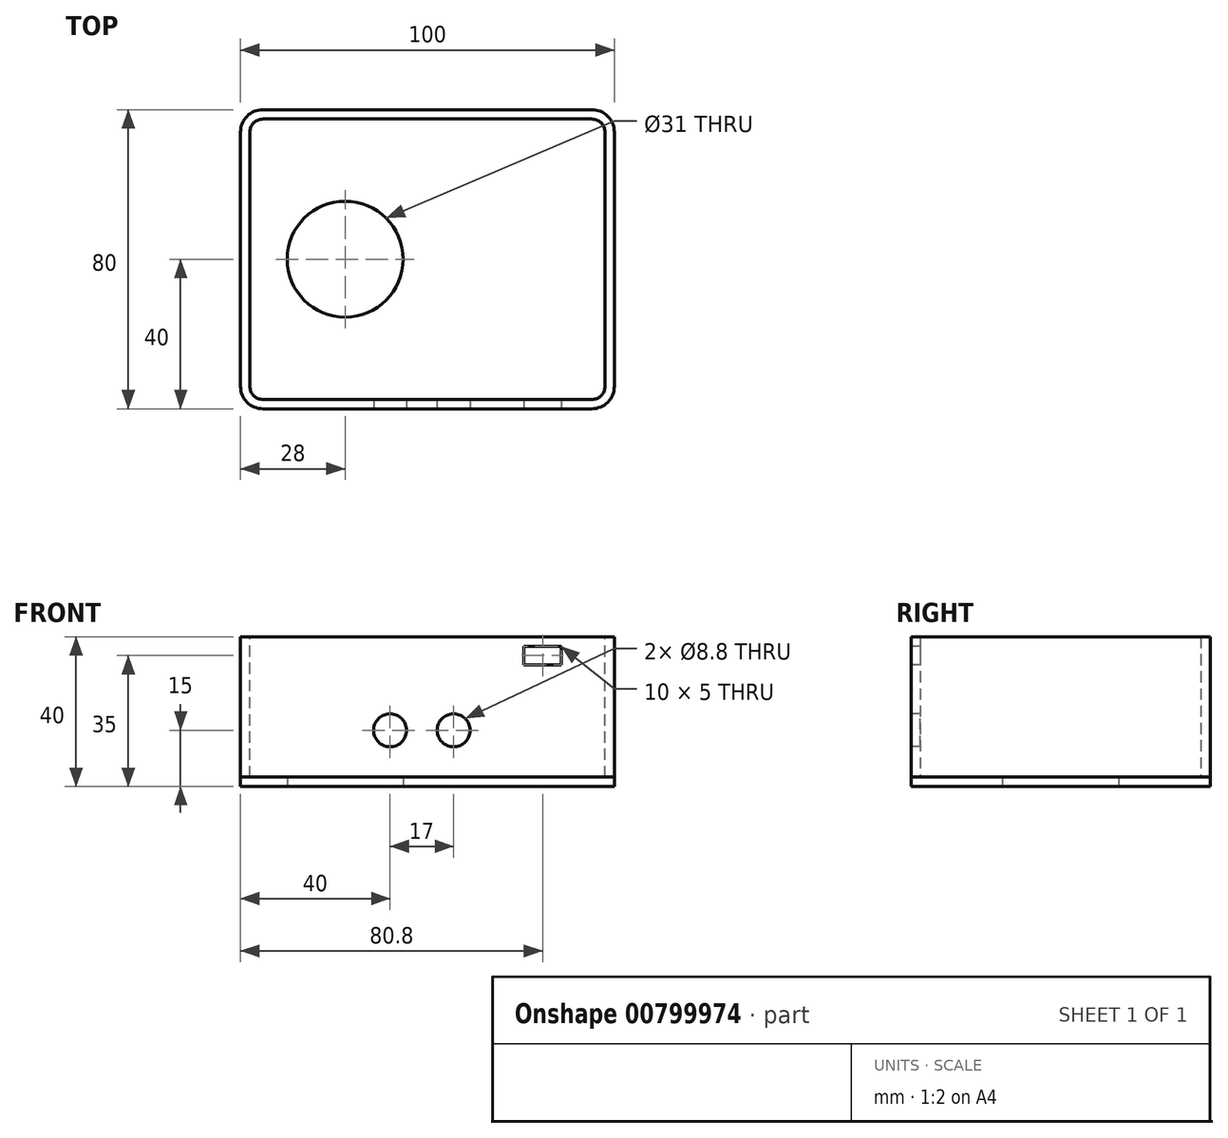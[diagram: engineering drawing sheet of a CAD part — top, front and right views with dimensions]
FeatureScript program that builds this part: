
annotation { "Feature Type Name" : "Feature", "Feature Type Description" : "" }
export const myFeature = defineFeature(function(context is Context, id is Id, definition is map)
    precondition{}
    {
        {
            var Q0;
            Q0=qCreatedBy(makeId("Top.planeOp"),FACE);
            var sketch = newSketch(context, id + "F0", { "sketchPlane" : qUnion([Q0])});
            skLineSegment(sketch, "E0.bottom", {"start": v(50, -40) * mm, "end": v(-50, -40) * mm});
            skLineSegment(sketch, "E0.top", {"start": v(50, 40) * mm, "end": v(-50, 40) * mm});
            skLineSegment(sketch, "E0.left", {"start": v(50, -40) * mm, "end": v(50, 40) * mm});
            skLineSegment(sketch, "E0.right", {"start": v(-50, -40) * mm, "end": v(-50, 40) * mm});
            skPoint(sketch, "E0.middle", {"position": v(0, 0) * mm});
            skSolve(sketch);
        }
        {
            var Q0;
            Q0 = qSketchRegion(id + "F0", true);
            extrude(context, id + "F1", {"entities" : qUnion([Q0]), "depth" : 40 * mm, "offsetDistance" : 25 * mm});
        }
        {
            var Q0;
            Q0=makeQuery(id+"F1.opExtrude","SWEPT_EDGE",EDGE,{"disambiguationData":[OSD([sQuery(id+"F0.wireOp",EDGE,"E0.bottom"),sQuery(id+"F0.wireOp",EDGE,"E0.right")])]});
            var Q1;
            Q1=makeQuery(id+"F1.opExtrude","SWEPT_EDGE",EDGE,{"disambiguationData":[OSD([sQuery(id+"F0.wireOp",EDGE,"E0.bottom"),sQuery(id+"F0.wireOp",EDGE,"E0.left")])]});
            var Q2;
            Q2=makeQuery(id+"F1.opExtrude","SWEPT_EDGE",EDGE,{"disambiguationData":[OSD([sQuery(id+"F0.wireOp",EDGE,"E0.top"),sQuery(id+"F0.wireOp",EDGE,"E0.left")])]});
            var Q3;
            Q3=makeQuery(id+"F1.opExtrude","SWEPT_EDGE",EDGE,{"disambiguationData":[OSD([sQuery(id+"F0.wireOp",EDGE,"E0.top"),sQuery(id+"F0.wireOp",EDGE,"E0.right")])]});
            fillet(context, id + "F2", {"entities" : qUnion([Q0, Q1, Q2, Q3]), "radius" : 6 * mm, "tangentPropagation" : true, "defaultsChanged" : false, "vertexSettings" : [], "allowEdgeOverflow" : false});
        }
        {
            var Q0;
            Q0=makeQuery(id+"F1.opExtrude","CAP_FACE",FACE,{"disambiguationData":[OSD([sQuery(id+"F0.wireOp",EDGE,"E0.bottom"),sQuery(id+"F0.wireOp",EDGE,"E0.top"),sQuery(id+"F0.wireOp",EDGE,"E0.left"),sQuery(id+"F0.wireOp",EDGE,"E0.right")])],"isStart":false});
            shell(context, id + "F3", {"entities" : qUnion([Q0]), "thickness" : 2.5 * mm});
        }
        {
            var Q0;
            Q0=qCreatedBy(makeId("Top.planeOp"),FACE);
            var sketch = newSketch(context, id + "F4", { "sketchPlane" : qUnion([Q0])});
            skPoint(sketch, "E1", {"position": v(-22, 0) * mm});
            skLineSegment(sketch, "E2.0.0", {"start": v(-44, 40) * mm, "end": v(44, 40) * mm});
            skArc(sketch, "E2.0.1", {"start": v(44, 40) * mm, "mid": v(48.24, 38.24) * mm, "end": v(50, 34) * mm});
            skLineSegment(sketch, "E2.0.2", {"start": v(50, 34) * mm, "end": v(50, -34) * mm});
            skArc(sketch, "E2.0.3", {"start": v(50, -34) * mm, "mid": v(48.24, -38.24) * mm, "end": v(44, -40) * mm});
            skLineSegment(sketch, "E2.0.4", {"start": v(44, -40) * mm, "end": v(-44, -40) * mm});
            skArc(sketch, "E2.0.5", {"start": v(-44, -40) * mm, "mid": v(-48.24, -38.24) * mm, "end": v(-50, -34) * mm});
            skLineSegment(sketch, "E2.0.6", {"start": v(-50, -34) * mm, "end": v(-50, 34) * mm});
            skArc(sketch, "E2.0.7", {"start": v(-50, 34) * mm, "mid": v(-48.24, 38.24) * mm, "end": v(-44, 40) * mm});
            skLineSegment(sketch, "E3", {"start": v(-22, 0) * mm, "end": v(-50, 0) * mm, "construction": true});
            skSolve(sketch);
        }
        {
            var Q0;
            Q0=sQuery(id+"F4.wireOp",VERTEX,"E1");
            var Q1;
            Q1=makeQuery(id+"F1.opExtrude","SWEPT_BODY",BODY,{"disambiguationData":[OSD([sQuery(id+"F0.wireOp",EDGE,"E0.bottom"),sQuery(id+"F0.wireOp",EDGE,"E0.top"),sQuery(id+"F0.wireOp",EDGE,"E0.left"),sQuery(id+"F0.wireOp",EDGE,"E0.right")])]});
            hole(context, id + "F5", {"style" : HoleStyle.SIMPLE, "endStyle" : HoleEndStyle.THROUGH, "oppositeDirection" : true, "holeDiameter" : 31 * mm, "majorDiameter" : 5 * mm, "isTappedThrough" : true, "tappedDepth" : 12 * mm, "tapClearance" : 3, "locations" : qUnion([Q0]), "scope" : qUnion([Q1])});
        }
        {
            var Q0;
            Q0=makeQuery(id+"F1.opExtrude","SWEPT_FACE",FACE,{"disambiguationData":[OSD([sQuery(id+"F0.wireOp",EDGE,"E0.bottom")])]});
            var sketch = newSketch(context, id + "F6", { "sketchPlane" : qUnion([Q0])});
            skPoint(sketch, "E4", {"position": v(7, 15) * mm});
            skPoint(sketch, "E5", {"position": v(-10, 15) * mm});
            skLineSegment(sketch, "E6", {"start": v(-10, 15) * mm, "end": v(7, 15) * mm, "construction": true});
            skLineSegment(sketch, "E7", {"start": v(7, 15) * mm, "end": v(7, 40) * mm, "construction": true});
            skLineSegment(sketch, "E8", {"start": v(7, 15) * mm, "end": v(44, 15) * mm, "construction": true});
            skSolve(sketch);
        }
        {
            var Q0;
            Q0=sQuery(id+"F6.wireOp",VERTEX,"E5");
            var Q1;
            Q1=sQuery(id+"F6.wireOp",VERTEX,"E4");
            var Q2;
            Q2=makeQuery(id+"F1.opExtrude","SWEPT_BODY",BODY,{"disambiguationData":[OSD([sQuery(id+"F0.wireOp",EDGE,"E0.bottom"),sQuery(id+"F0.wireOp",EDGE,"E0.top"),sQuery(id+"F0.wireOp",EDGE,"E0.left"),sQuery(id+"F0.wireOp",EDGE,"E0.right")])]});
            hole(context, id + "F7", {"style" : HoleStyle.SIMPLE, "endStyle" : HoleEndStyle.BLIND, "standardTappedOrClearance" : lookupTablePath({ "standard" : "ISO", "fit" : "Normal", "size" : "M8", "type" : "Clearance" }), "standardBlindInLast" : lookupTablePath({ "fit" : "Standard", "standard" : "ISO", "size" : "M8", "type" : "Clearance" }), "holeDiameter" : 8.8 * mm, "majorDiameter" : 5 * mm, "holeDepth" : 5 * mm, "isTappedThrough" : true, "tappedDepth" : 12 * mm, "tapClearance" : 3, "locations" : qUnion([Q0, Q1]), "scope" : qUnion([Q2])});
        }
        {
            var Q0;
            Q0=makeQuery(id+"F1.opExtrude","SWEPT_FACE",FACE,{"disambiguationData":[OSD([sQuery(id+"F0.wireOp",EDGE,"E0.bottom")])]});
            var sketch = newSketch(context, id + "F8", { "sketchPlane" : qUnion([Q0])});
            skLineSegment(sketch, "E9.bottom", {"start": v(35.8, 32.5) * mm, "end": v(25.8, 32.5) * mm});
            skLineSegment(sketch, "E9.top", {"start": v(35.8, 37.5) * mm, "end": v(25.8, 37.5) * mm});
            skLineSegment(sketch, "E9.left", {"start": v(35.8, 32.5) * mm, "end": v(35.8, 37.5) * mm});
            skLineSegment(sketch, "E9.right", {"start": v(25.8, 32.5) * mm, "end": v(25.8, 37.5) * mm});
            skPoint(sketch, "E9.middle", {"position": v(30.8, 35) * mm});
            skLineSegment(sketch, "E10", {"start": v(30.8, 15) * mm, "end": v(7, 15) * mm, "construction": true});
            skLineSegment(sketch, "E11", {"start": v(30.8, 15) * mm, "end": v(30.8, 35) * mm, "construction": true});
            skSolve(sketch);
        }
        {
            var Q0;
            Q0 = qSketchRegion(id + "F8", true);
            extrude(context, id + "F9", {"entities" : qUnion([Q0]), "operationType" : NewBodyOperationType.REMOVE, "endBound" : BoundingType.UP_TO_NEXT, "oppositeDirection" : true, "depth" : 25 * mm, "offsetDistance" : 25 * mm});
        }
        {
            var Q0;
            Q0 = qSketchRegion(id + "F0", true);
            extrude(context, id + "F10", {"entities" : qUnion([Q0]), "depth" : 2.5 * mm, "offsetDistance" : 25 * mm});
        }
        {
            var Q0;
            Q0=makeQuery(id+"F10.opExtrude","SWEPT_EDGE",EDGE,{"disambiguationData":[OSD([sQuery(id+"F0.wireOp",EDGE,"E0.bottom"),sQuery(id+"F0.wireOp",EDGE,"E0.left")])]});
            var Q1;
            Q1=makeQuery(id+"F10.opExtrude","SWEPT_EDGE",EDGE,{"disambiguationData":[OSD([sQuery(id+"F0.wireOp",EDGE,"E0.top"),sQuery(id+"F0.wireOp",EDGE,"E0.left")])]});
            var Q2;
            Q2=makeQuery(id+"F10.opExtrude","SWEPT_EDGE",EDGE,{"disambiguationData":[OSD([sQuery(id+"F0.wireOp",EDGE,"E0.bottom"),sQuery(id+"F0.wireOp",EDGE,"E0.right")])]});
            var Q3;
            Q3=makeQuery(id+"F10.opExtrude","SWEPT_EDGE",EDGE,{"disambiguationData":[OSD([sQuery(id+"F0.wireOp",EDGE,"E0.top"),sQuery(id+"F0.wireOp",EDGE,"E0.right")])]});
            fillet(context, id + "F11", {"entities" : qUnion([Q0, Q1, Q2, Q3]), "radius" : 6 * mm, "tangentPropagation" : true, "defaultsChanged" : false, "vertexSettings" : [], "allowEdgeOverflow" : false});
        }
    });
